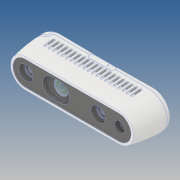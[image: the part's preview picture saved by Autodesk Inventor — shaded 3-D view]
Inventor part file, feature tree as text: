
AUTODESK INVENTOR PART (.ipt)
format: ipt  version: 2020 (Build 240168000, 168)  size: 1,153,024 bytes
history: imported  units: mm
features: other x9, projected_geometry x3, sketch x1, imported_body x1
ambient origin geometry x8: Origin, YZ Plane, XZ Plane, XY Plane, X Axis, Y Axis, Z Axis, Center Point
bodies: Solid1 (imported_parasolid), Solid2 (imported_parasolid), Solid3 (imported_parasolid), Solid4 (imported_parasolid), Solid5 (imported_parasolid), Solid6 (imported_parasolid), Solid7 (imported_parasolid), Solid8 (imported_parasolid)
feature tree (14):
  sketch  "Sketch1"
  other  "РабПлоскость1"
  projected_geometry  "Projected Loop1"
  projected_geometry  "Projected Loop2"
  projected_geometry  "Projected Loop3"
  other  "Cut-Extrude-Thin2[2]"
  other  "LPattern6[1]"
  other  "LPattern6[2]"
  other  "LPattern6[3]"
  other  "LPattern6[4]"
  other  "LPattern6[5]"
  other  "Dome2"
  other  "Boss-Extrude6"
  imported_body  NMx_Import_Brep_tag  [imported B-rep: ~17 faces, bbox_mm=None]
